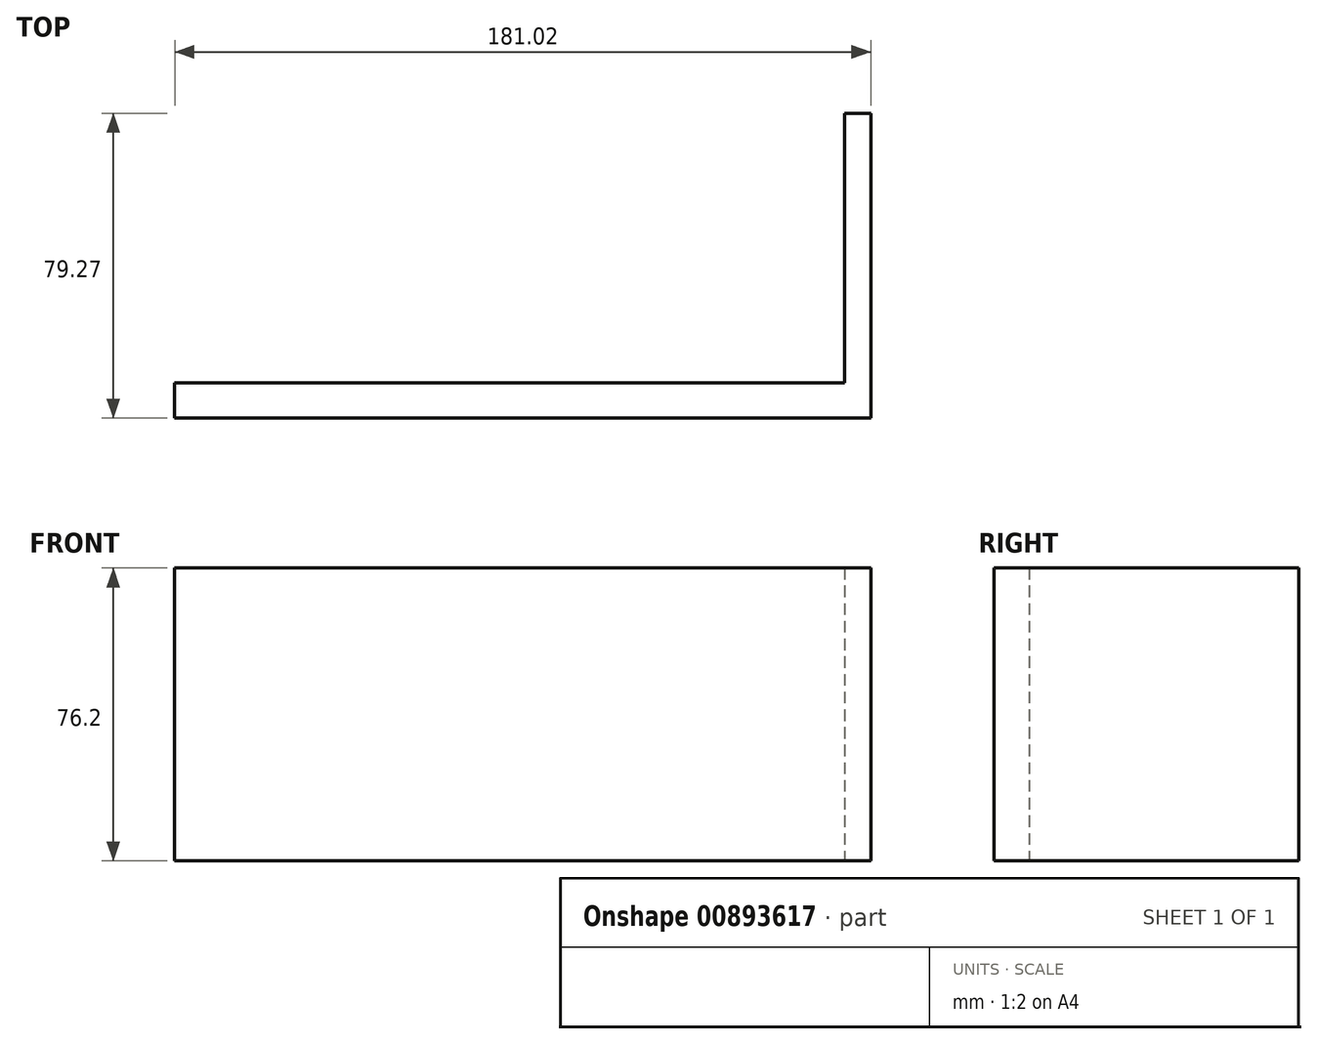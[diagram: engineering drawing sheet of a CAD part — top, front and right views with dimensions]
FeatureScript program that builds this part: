
annotation { "Feature Type Name" : "Feature", "Feature Type Description" : "" }
export const myFeature = defineFeature(function(context is Context, id is Id, definition is map)
    precondition{}
    {
        {
            var Q0;
            Q0=qCreatedBy(makeId("Top.planeOp"),FACE);
            var sketch = newSketch(context, id + "F0", { "sketchPlane" : qUnion([Q0])});
            skLineSegment(sketch, "E0", {"start": v(81.78, 43.18) * mm, "end": v(81.78, -26.92) * mm});
            skLineSegment(sketch, "E1", {"start": v(81.78, 43.18) * mm, "end": v(88.59, 43.18) * mm});
            skLineSegment(sketch, "E2", {"start": v(88.59, 43.18) * mm, "end": v(88.59, -36.09) * mm});
            skLineSegment(sketch, "E3", {"start": v(88.59, -36.09) * mm, "end": v(-92.43, -36.09) * mm});
            skLineSegment(sketch, "E4", {"start": v(81.78, -26.92) * mm, "end": v(-92.43, -26.92) * mm});
            skLineSegment(sketch, "E5", {"start": v(-92.43, -26.92) * mm, "end": v(-92.43, -36.09) * mm});
            skSolve(sketch);
        }
        {
            var Q0;
            Q0=qCreatedBy(makeId("Top.planeOp"),FACE);
            var sketch = newSketch(context, id + "F1", { "sketchPlane" : qUnion([Q0])});
            skLineSegment(sketch, "E6", {"start": v(-79.12, -36.38) * mm, "end": v(-79.12, -62.41) * mm});
            skLineSegment(sketch, "E7", {"start": v(-79.12, -62.41) * mm, "end": v(82.08, -62.41) * mm});
            skLineSegment(sketch, "E8", {"start": v(82.08, -62.41) * mm, "end": v(82.08, -37.27) * mm});
            skSolve(sketch);
        }
        {
            var Q0;
            Q0 = qSketchRegion(id + "F0", true);
            extrude(context, id + "F2", {"entities" : qUnion([Q0]), "depth" : 76.2 * mm, "offsetDistance" : 25.4 * mm});
        }
        {
            var Q0;
            Q0 = qSketchRegion(id + "F0", true);
            extrude(context, id + "F3", {"entities" : qUnion([Q0]), "operationType" : NewBodyOperationType.ADD, "depth" : 76.2 * mm, "offsetDistance" : 25.4 * mm});
        }
        {
            var Q0;
            Q0=sQuery(id+"F1.wireOp",EDGE,"E7");
            var Q1;
            Q1=sQuery(id+"F1.wireOp",EDGE,"E8");
            var Q2;
            Q2=sQuery(id+"F1.wireOp",EDGE,"E6");
            extrude(context, id + "F4", {"bodyType" : ToolBodyType.SURFACE, "surfaceEntities" : qUnion([Q0, Q1, Q2]), "depth" : 76.2 * mm, "offsetDistance" : 25.4 * mm});
        }
    });
